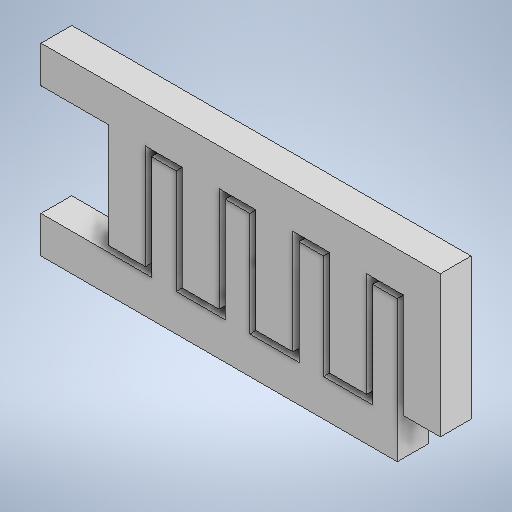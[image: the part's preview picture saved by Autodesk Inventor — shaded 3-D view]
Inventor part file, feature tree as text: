
AUTODESK INVENTOR PART (.ipt)
format: ipt  version: 2025.2 (Build 292293000, 293)  size: 262,656 bytes
history: native  units: mm
features: extrude x1, sketch x1
ambient origin geometry x8: Origin, YZ Plane, XZ Plane, XY Plane, X Axis, Y Axis, Z Axis, Center Point
bodies: Solid1 (feature_tree)
feature tree (2):
  extrude  "Extrusion1"  Depth=6.0mm
  sketch  "Sketch1"  dims[d92=5.0mm d93=0.0mm d119=6.0mm d120=6.0mm d121=17.0mm d122=23.0mm d124=65.0mm d127=31.390887mm d128=71.564748mm d129=6.0mm d131=6.0mm d132=1.0mm]
